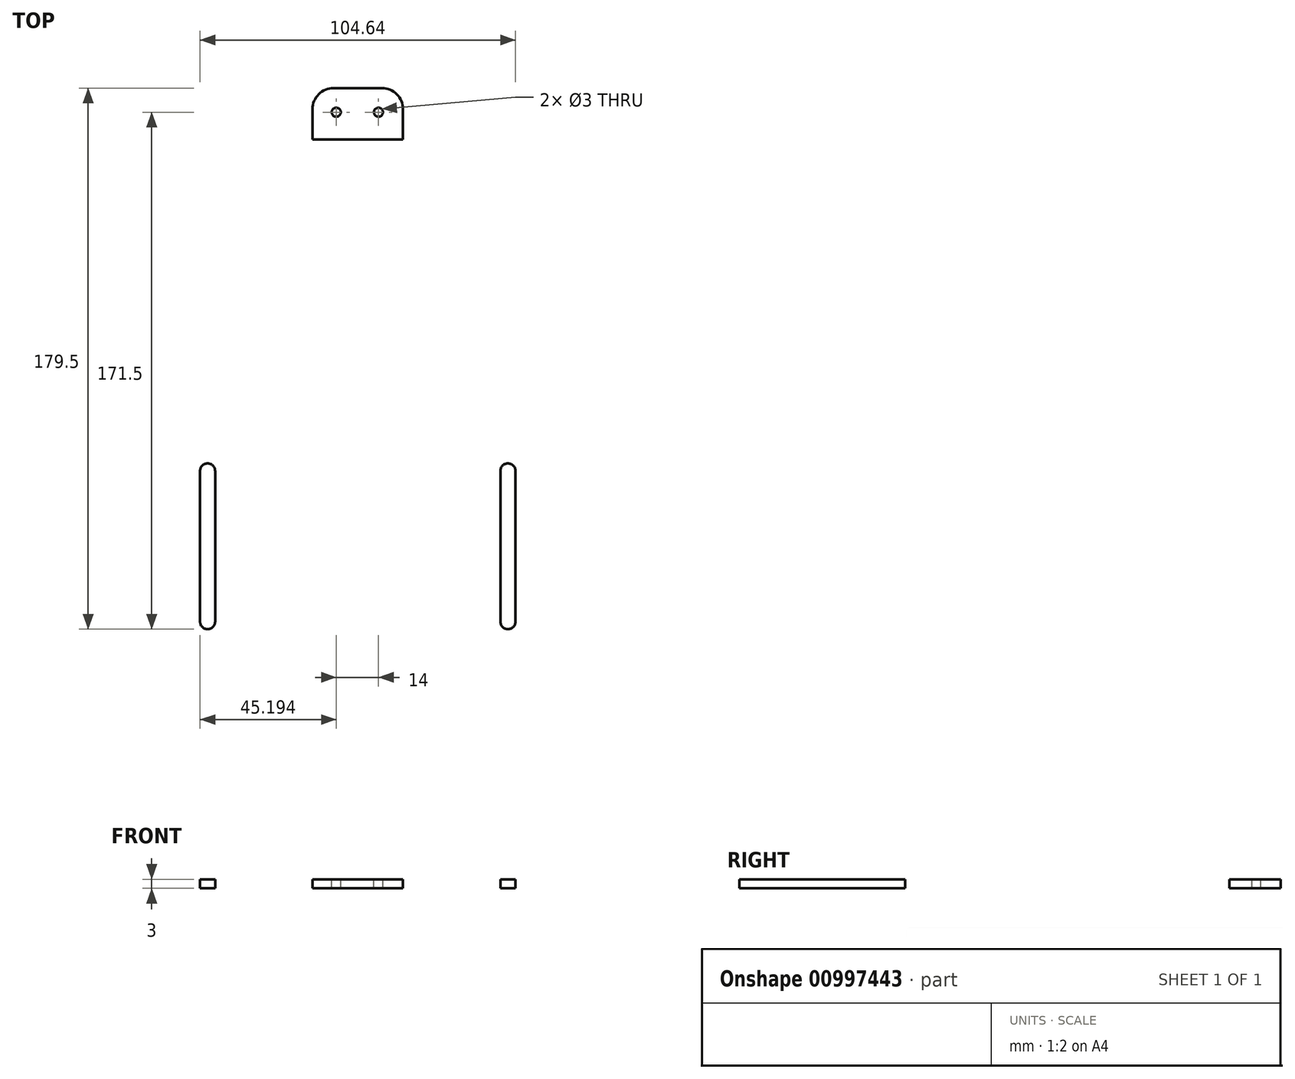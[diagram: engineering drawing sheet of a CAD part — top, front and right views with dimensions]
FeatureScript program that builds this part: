
annotation { "Feature Type Name" : "Feature", "Feature Type Description" : "" }
export const myFeature = defineFeature(function(context is Context, id is Id, definition is map)
    precondition{}
    {
        {
            var Q0;
            Q0=qCreatedBy(makeId("Top.planeOp"),FACE);
            var sketch = newSketch(context, id + "F0", { "sketchPlane" : qUnion([Q0])});
            skLineSegment(sketch, "E0.bottom", {"start": v(0, 0) * mm, "end": v(48, 0) * mm});
            skLineSegment(sketch, "E0.top", {"start": v(0, 165) * mm, "end": v(48, 165) * mm});
            skLineSegment(sketch, "E0.left", {"start": v(0, 0) * mm, "end": v(0, 165) * mm});
            skLineSegment(sketch, "E0.right", {"start": v(48, 0) * mm, "end": v(48, 165) * mm});
            skSolve(sketch);
        }
        {
            var Q0;
            Q0 = qSketchRegion(id + "F0", true);
            extrude(context, id + "F1", {"entities" : qUnion([Q0]), "depth" : 3 * mm, "offsetDistance" : 25 * mm});
        }
        {
            var Q0;
            Q0=makeQuery(id+"F1.opExtrude","CAP_FACE",FACE,{"disambiguationData":[OSD([sQuery(id+"F0.wireOp",EDGE,"E0.bottom"),sQuery(id+"F0.wireOp",EDGE,"E0.top"),sQuery(id+"F0.wireOp",EDGE,"E0.left"),sQuery(id+"F0.wireOp",EDGE,"E0.right")])],"isStart":false});
            var sketch = newSketch(context, id + "F2", { "sketchPlane" : qUnion([Q0])});
            skLineSegment(sketch, "E1.bottom", {"start": v(48, 0) * mm, "end": v(53.39, 0) * mm});
            skLineSegment(sketch, "E1.top", {"start": v(48, 60) * mm, "end": v(53.39, 60) * mm});
            skLineSegment(sketch, "E1.left", {"start": v(48, 0) * mm, "end": v(48, 60) * mm});
            skLineSegment(sketch, "E1.right", {"start": v(53.39, 0) * mm, "end": v(53.39, 60) * mm});
            skLineSegment(sketch, "E2", {"start": v(50.7, 57.73) * mm, "end": v(50.7, 7.73) * mm});
            skPoint(sketch, "E2.startSnap0", {"position": v(50.7, 60) * mm});
            skPoint(sketch, "E2.endSnap0", {"position": v(50.7, 0) * mm});
            skSolve(sketch);
        }
        {
            var Q0;
            Q0 = qSketchRegion(id + "F2", true);
            var Q1;
            Q1=makeQuery(id+"F1.opExtrude","CAP_FACE",FACE,{"disambiguationData":[OSD([sQuery(id+"F0.wireOp",EDGE,"E0.bottom"),sQuery(id+"F0.wireOp",EDGE,"E0.top"),sQuery(id+"F0.wireOp",EDGE,"E0.left"),sQuery(id+"F0.wireOp",EDGE,"E0.right")])],"isStart":false});
            extrude(context, id + "F3", {"entities" : qUnion([Q0, Q1]), "operationType" : NewBodyOperationType.ADD, "oppositeDirection" : true, "depth" : 3 * mm, "offsetDistance" : 25 * mm});
        }
        {
            var Q0;
            Q0=makeQuery(id+"F3.boolean.opBoolean","MERGE",FACE,{"derivedFrom":[makeQuery(id+"F1.opExtrude","CAP_FACE",FACE,{"disambiguationData":[OSD([sQuery(id+"F0.wireOp",EDGE,"E0.bottom"),sQuery(id+"F0.wireOp",EDGE,"E0.top"),sQuery(id+"F0.wireOp",EDGE,"E0.left"),sQuery(id+"F0.wireOp",EDGE,"E0.right")])],"isStart":false}),makeQuery(id+"F3.opExtrude","CAP_FACE",FACE,{"disambiguationData":[OSD([sQuery(id+"F2.wireOp",EDGE,"E1.bottom"),sQuery(id+"F2.wireOp",EDGE,"E1.top"),sQuery(id+"F2.wireOp",EDGE,"E1.left"),sQuery(id+"F2.wireOp",EDGE,"E1.right")])],"isStart":true})]});
            var sketch = newSketch(context, id + "F4", { "sketchPlane" : qUnion([Q0])});
            skLineSegment(sketch, "E3.bottom", {"start": v(0, 165) * mm, "end": v(15, 165) * mm});
            skLineSegment(sketch, "E3.top", {"start": v(0, 182) * mm, "end": v(15, 182) * mm});
            skLineSegment(sketch, "E3.left", {"start": v(0, 165) * mm, "end": v(0, 182) * mm});
            skLineSegment(sketch, "E3.right", {"start": v(15, 165) * mm, "end": v(15, 182) * mm});
            skSolve(sketch);
        }
        {
            var Q0;
            Q0=makeQuery(id+"F4.imprint","IMPRINT",FACE,{"disambiguationData":[TD([[makeQuery(id+"F4.imprint","IMPRINT",EDGE,{"derivedFrom":sQuery(id+"F4.wireOp",EDGE,"E3.bottom")}),1.0]])]});
            extrude(context, id + "F5", {"entities" : qUnion([Q0]), "operationType" : NewBodyOperationType.ADD, "oppositeDirection" : true, "depth" : 3 * mm, "offsetDistance" : 25 * mm});
        }
        {
            var Q0;
            Q0=makeQuery(id+"F5.opExtrude","SWEPT_EDGE",EDGE,{"disambiguationData":[OSD([sQuery(id+"F4.wireOp",EDGE,"E3.top"),sQuery(id+"F4.wireOp",EDGE,"E3.right")])]});
            fillet(context, id + "F6", {"entities" : qUnion([Q0]), "radius" : 7 * mm, "tangentPropagation" : true, "allowEdgeOverflow" : false});
        }
        {
            var Q0;
            {var subQ2=sQuery(id+"F4.wireOp",EDGE,"E3.bottom");Q0=makeQuery(id+"F4.imprint","IMPRINT",FACE,{"disambiguationData":[TD([[makeQuery(id+"F4.imprint","IMPRINT",EDGE,{"derivedFrom":subQ2}),-1.0]])]});}
            var sketch = newSketch(context, id + "F7", { "sketchPlane" : qUnion([Q0])});
            skLineSegment(sketch, "E4", {"start": v(49.82, 55) * mm, "end": v(49.82, 5) * mm});
            skArc(sketch, "E5.0.startCap", {"start": v(47.32, 55) * mm, "mid": v(49.82, 57.5) * mm, "end": v(52.32, 55) * mm});
            skArc(sketch, "E5.0.endCap", {"start": v(52.32, 5) * mm, "mid": v(49.82, 2.5) * mm, "end": v(47.32, 5) * mm});
            skLineSegment(sketch, "E5.0.left", {"start": v(52.32, 55) * mm, "end": v(52.32, 5) * mm});
            skLineSegment(sketch, "E5.0.right", {"start": v(47.32, 55) * mm, "end": v(47.32, 5) * mm});
            skSolve(sketch);
        }
        {
            var Q0;
            Q0=makeQuery(id+"F7.imprint","IMPRINT",FACE,{"disambiguationData":[TD([[makeQuery(id+"F7.imprint","IMPRINT",EDGE,{"derivedFrom":sQuery(id+"F7.wireOp",EDGE,"E5.0.startCap")}),-1.0]])]});
            extrude(context, id + "F8", {"entities" : qUnion([Q0]), "operationType" : NewBodyOperationType.REMOVE, "oppositeDirection" : true, "depth" : 61.8 * mm, "offsetDistance" : 25 * mm});
        }
        {
            var Q0;
            {var subQ2=sQuery(id+"F4.wireOp",EDGE,"E3.bottom");Q0=makeQuery(id+"F4.imprint","IMPRINT",FACE,{"disambiguationData":[TD([[makeQuery(id+"F4.imprint","IMPRINT",EDGE,{"derivedFrom":subQ2}),-1.0]])]});}
            var sketch = newSketch(context, id + "F9", { "sketchPlane" : qUnion([Q0])});
            skLineSegment(sketch, "E6", {"start": v(29.32, 47) * mm, "end": v(29.32, 15) * mm});
            skSolve(sketch);
        }
        {
            var Q0;
            Q0=sQuery(id+"F9.wireOp",VERTEX,"E6.end");
            var Q1;
            Q1=sQuery(id+"F9.wireOp",VERTEX,"E6.start");
            var Q2;
            Q2=makeQuery(id+"F1.opExtrude","SWEPT_BODY",BODY,{"disambiguationData":[OSD([sQuery(id+"F0.wireOp",EDGE,"E0.bottom"),sQuery(id+"F0.wireOp",EDGE,"E0.top"),sQuery(id+"F0.wireOp",EDGE,"E0.left"),sQuery(id+"F0.wireOp",EDGE,"E0.right")])]});
            hole(context, id + "F10", {"style" : HoleStyle.SIMPLE, "endStyle" : HoleEndStyle.THROUGH, "holeDiameter" : 3 * mm, "majorDiameter" : 5 * mm, "isTappedThrough" : true, "tappedDepth" : 12 * mm, "tapClearance" : 3, "locations" : qUnion([Q0, Q1]), "scope" : qUnion([Q2])});
        }
        {
            var Q0;
            Q0=makeQuery(id+"F4.imprint","IMPRINT",FACE,{"disambiguationData":[TD([[makeQuery(id+"F4.imprint","IMPRINT",EDGE,{"derivedFrom":sQuery(id+"F4.wireOp",EDGE,"E3.bottom")}),1.0]])]});
            var sketch = newSketch(context, id + "F11", { "sketchPlane" : qUnion([Q0])});
            skSolve(sketch);
        }
        {
            var Q0;
            Q0=makeQuery(id+"F11.imprint","IMPRINT",FACE,{"disambiguationData":[TD([[makeQuery(id+"F11.imprint","IMPRINT",EDGE,{"derivedFrom":makeQuery(id+"F4.imprint","IMPRINT",EDGE,{"derivedFrom":sQuery(id+"F4.wireOp",EDGE,"E3.bottom")})}),1.0]])]});
            var sketch = newSketch(context, id + "F12", { "sketchPlane" : qUnion([Q0])});
            skSolve(sketch);
        }
        {
            var Q0;
            Q0=makeQuery(id+"F1.opExtrude","SWEPT_BODY",BODY,{"disambiguationData":[OSD([sQuery(id+"F0.wireOp",EDGE,"E0.bottom"),sQuery(id+"F0.wireOp",EDGE,"E0.top"),sQuery(id+"F0.wireOp",EDGE,"E0.left"),sQuery(id+"F0.wireOp",EDGE,"E0.right")])]});
            var Q1;
            Q1=qCreatedBy(makeId("Right.planeOp"),FACE);
            mirror(context, id + "F13", {"operationType" : NewBodyOperationType.ADD, "entities" : qUnion([Q0]), "mirrorPlane" : qUnion([Q1])});
        }
        {
            var Q0;
            Q0=makeQuery(id+"F12.imprint","IMPRINT",FACE,{"disambiguationData":[TD([[makeQuery(id+"F12.imprint","IMPRINT",EDGE,{"derivedFrom":makeQuery(id+"F11.imprint","IMPRINT",EDGE,{"derivedFrom":makeQuery(id+"F4.imprint","IMPRINT",EDGE,{"derivedFrom":sQuery(id+"F4.wireOp",EDGE,"E3.bottom")})})}),1.0]])]});
            var sketch = newSketch(context, id + "F14", { "sketchPlane" : qUnion([Q0])});
            skLineSegment(sketch, "E7", {"start": v(6.87, 174) * mm, "end": v(-7.13, 174) * mm});
            skSolve(sketch);
        }
        {
            var Q0;
            Q0=sQuery(id+"F14.wireOp",VERTEX,"E7.start");
            var Q1;
            Q1=sQuery(id+"F14.wireOp",VERTEX,"E7.end");
            var Q2;
            Q2=makeQuery(id+"F1.opExtrude","SWEPT_BODY",BODY,{"disambiguationData":[OSD([sQuery(id+"F0.wireOp",EDGE,"E0.bottom"),sQuery(id+"F0.wireOp",EDGE,"E0.top"),sQuery(id+"F0.wireOp",EDGE,"E0.left"),sQuery(id+"F0.wireOp",EDGE,"E0.right")])]});
            hole(context, id + "F15", {"style" : HoleStyle.SIMPLE, "endStyle" : HoleEndStyle.THROUGH, "holeDiameter" : 3 * mm, "majorDiameter" : 5 * mm, "isTappedThrough" : true, "tappedDepth" : 12 * mm, "tapClearance" : 3, "locations" : qUnion([Q0, Q1]), "scope" : qUnion([Q2])});
        }
        {
            var Q0;
            {var subQ2=sQuery(id+"F4.wireOp",EDGE,"E3.bottom");Q0=makeQuery(id+"F4.imprint","IMPRINT",FACE,{"disambiguationData":[TD([[makeQuery(id+"F4.imprint","IMPRINT",EDGE,{"derivedFrom":subQ2}),-1.0]])]});}
            var sketch = newSketch(context, id + "F16", { "sketchPlane" : qUnion([Q0])});
            skLineSegment(sketch, "E8", {"start": v(21.83, 157) * mm, "end": v(21.83, 92) * mm});
            skSolve(sketch);
        }
        {
            var Q0;
            Q0=sQuery(id+"F16.wireOp",VERTEX,"E8.start");
            var Q1;
            Q1=makeQuery(id+"F1.opExtrude","SWEPT_BODY",BODY,{"disambiguationData":[OSD([sQuery(id+"F0.wireOp",EDGE,"E0.bottom"),sQuery(id+"F0.wireOp",EDGE,"E0.top"),sQuery(id+"F0.wireOp",EDGE,"E0.left"),sQuery(id+"F0.wireOp",EDGE,"E0.right")])]});
            hole(context, id + "F17", {"style" : HoleStyle.SIMPLE, "endStyle" : HoleEndStyle.THROUGH, "holeDiameter" : 3 * mm, "majorDiameter" : 5 * mm, "isTappedThrough" : true, "tappedDepth" : 12 * mm, "tapClearance" : 3, "locations" : qUnion([Q0]), "scope" : qUnion([Q1])});
        }
        {
            var Q0;
            {var subQ0=sQuery(id+"F0.wireOp",EDGE,"E0.right");var subQ1=sQuery(id+"F0.wireOp",EDGE,"E0.left");var subQ2=sQuery(id+"F0.wireOp",EDGE,"E0.top");var subQ3=sQuery(id+"F0.wireOp",EDGE,"E0.bottom");var subQ4=makeQuery(id+"F5.boolean.opBoolean","MERGE",FACE,{"derivedFrom":[makeQuery(id+"F3.boolean.opBoolean","MERGE",FACE,{"derivedFrom":[makeQuery(id+"F1.opExtrude","CAP_FACE",FACE,{"disambiguationData":[OSD([subQ3,subQ2,subQ1,subQ0])],"isStart":false}),makeQuery(id+"F3.opExtrude","CAP_FACE",FACE,{"disambiguationData":[OSD([subQ3,subQ2,subQ1,subQ0])],"isStart":true}),makeQuery(id+"F3.opExtrude","CAP_FACE",FACE,{"disambiguationData":[OSD([sQuery(id+"F2.wireOp",EDGE,"E1.bottom"),sQuery(id+"F2.wireOp",EDGE,"E1.top"),sQuery(id+"F2.wireOp",EDGE,"E1.left"),sQuery(id+"F2.wireOp",EDGE,"E1.right")])],"isStart":true})]}),makeQuery(id+"F5.opExtrude","CAP_FACE",FACE,{"disambiguationData":[OSD([sQuery(id+"F4.wireOp",EDGE,"E3.bottom"),sQuery(id+"F4.wireOp",EDGE,"E3.top"),sQuery(id+"F4.wireOp",EDGE,"E3.left"),sQuery(id+"F4.wireOp",EDGE,"E3.right")])],"isStart":true})]});Q0=makeQuery(id+"F13.boolean.opBoolean","MERGE",FACE,{"derivedFrom":[subQ4,makeQuery(id+"F13.opPattern","COPY",FACE,{"derivedFrom":subQ4,"instanceName":"1"})]});}
            var sketch = newSketch(context, id + "F18", { "sketchPlane" : qUnion([Q0])});
            skLineSegment(sketch, "E9", {"start": v(-27.47, 158) * mm, "end": v(-27.47, 73) * mm});
            skSolve(sketch);
        }
        {
            var Q0;
            Q0=sQuery(id+"F18.wireOp",VERTEX,"E9.end");
            var Q1;
            Q1=sQuery(id+"F18.wireOp",VERTEX,"E9.start");
            var Q2;
            Q2=makeQuery(id+"F1.opExtrude","SWEPT_BODY",BODY,{"disambiguationData":[OSD([sQuery(id+"F0.wireOp",EDGE,"E0.bottom"),sQuery(id+"F0.wireOp",EDGE,"E0.top"),sQuery(id+"F0.wireOp",EDGE,"E0.left"),sQuery(id+"F0.wireOp",EDGE,"E0.right")])]});
            hole(context, id + "F19", {"style" : HoleStyle.SIMPLE, "endStyle" : HoleEndStyle.THROUGH, "holeDiameter" : 3 * mm, "majorDiameter" : 5 * mm, "isTappedThrough" : true, "tappedDepth" : 12 * mm, "tapClearance" : 3, "locations" : qUnion([Q0, Q1]), "scope" : qUnion([Q2])});
        }
        {
            var Q0;
            {var subQ2=sQuery(id+"F4.wireOp",EDGE,"E3.bottom");Q0=makeQuery(id+"F4.imprint","IMPRINT",FACE,{"disambiguationData":[TD([[makeQuery(id+"F4.imprint","IMPRINT",EDGE,{"derivedFrom":subQ2}),-1.0]])]});}
            var sketch = newSketch(context, id + "F20", { "sketchPlane" : qUnion([Q0])});
            skLineSegment(sketch, "E10", {"start": v(22.16, 158.66) * mm, "end": v(22.16, 93.66) * mm});
            skLineSegment(sketch, "E11", {"start": v(39, 74.2) * mm, "end": v(2, 74.2) * mm});
            skSolve(sketch);
        }
        {
            var Q0;
            Q0=sQuery(id+"F20.wireOp",VERTEX,"E11.start");
            var Q1;
            Q1=makeQuery(id+"F1.opExtrude","SWEPT_BODY",BODY,{"disambiguationData":[OSD([sQuery(id+"F0.wireOp",EDGE,"E0.bottom"),sQuery(id+"F0.wireOp",EDGE,"E0.top"),sQuery(id+"F0.wireOp",EDGE,"E0.left"),sQuery(id+"F0.wireOp",EDGE,"E0.right")])]});
            hole(context, id + "F21", {"style" : HoleStyle.SIMPLE, "endStyle" : HoleEndStyle.THROUGH, "holeDiameter" : 3 * mm, "majorDiameter" : 5 * mm, "isTappedThrough" : true, "tappedDepth" : 12 * mm, "tapClearance" : 3, "locations" : qUnion([Q0]), "scope" : qUnion([Q1])});
        }
    });
